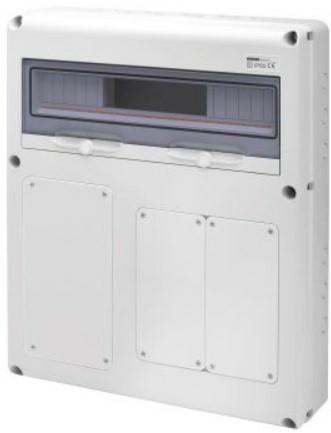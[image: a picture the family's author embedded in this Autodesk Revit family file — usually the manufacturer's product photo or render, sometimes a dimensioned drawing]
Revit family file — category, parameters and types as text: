
# Revit family: Building-IEC309Boards-GEWISS-68QDIN-DISTRIBUTION-BOARD-20MOD_3SOCKET-OUTLETS_IB_VERT
name_source: partatom
category: Apparecchi elettrici
units: mm (PartAtom-declared; Revit-internal decimal feet)

## family parameters
Condiviso = No
Host = Superficie
Mantenere orientamento annotazione = Sì
Punto di calcolo locali = Sì
Quota connettore circolare = Usa diametro
Taglio con vuoti quando caricato = No
Tipo di parte = Normale

## types (1)
- GW68022N - Q-DIN 20M 1S.O.BL.63A2S.O.BL.16/32A IP65
    Accordance with Standards = EN 60208 - EN 60670-1 - IEC 60670-24
    Catalogue = BUILDING
    Catalogue Range = 68 QDIN
    Colour = Grey RAL 7035
    Descrizione = Q-DIN 20M 1S.O.BL.63A2S.O.BL.16/32A IP65
    Dispersible power A (W) = 30
    Dispersible power B (W) = 92
    EAN code = 8011564744899
    Electrocod = 2242
    Glow Wire Test = 650°C
    Houseable socket = 1 IB Vert. 63A IP67 + 2 IB Vert. 16/32A IP67
    IDF = 0a978d39-9037-424a-8be2-c3a2fb2c057e
    IDT = c5faa6ce-0638-4a66-bbf1-3e08dc7c6100
    IP degree = IP65
    Immagine tipo = GW68022N.jpg
    Installation type = Surface-mounting
    Insulation class = II
    L_Moduli = 380 mm  [stored 1.24672 ft]
    Modello = GW68022N
    N_Moduli = 20 mm  [stored 0.0656168 ft]
    No. IB socket-outlets houseable = 1 IB Vert. 63A IP67 + 2 IB Vert. 16/32A IP67
    No. of blank lids supplied = 1 IB 16/32A
    No. of modules EN 50022 = 20
    No. of provided blank lids = 1 IB 16/32A
    Operating temperature: = -25 +40 °C
    POMELLO = bianco
    PRESA = rosso
    Produttore = GEWISS S.p.A.
    Prospetto di default = 1219 mm
    SEO = Board
    STRUTTURA = RAL - 7035
    STRUTTURA ALTA = Poche
    Shock resistance = IK08
    Spostamento_S = 1000 mm  [stored 3.28084 ft]
    Technical sheet = https://www.gewiss.com
    Thermo-pressure with ball = 70
    URL = https://www.gewiss.com
    VETRO = Vetro
    Version file RFA = 21.5
    Version type = Empty
    Working temperature = -25 ÷ +40 °C

note: source unit labels omitted for Thermo-pressure with ball — the stored unit's dimension contradicts the parameter name (converter mislabeling)

note: [stored X ft] marks values corroborated as IEEE doubles in the binary element streams (Revit-internal decimal feet)

## geometry (parser evidence)
native form markers: Sweep x5
no freeform markers — native parametric forms only
